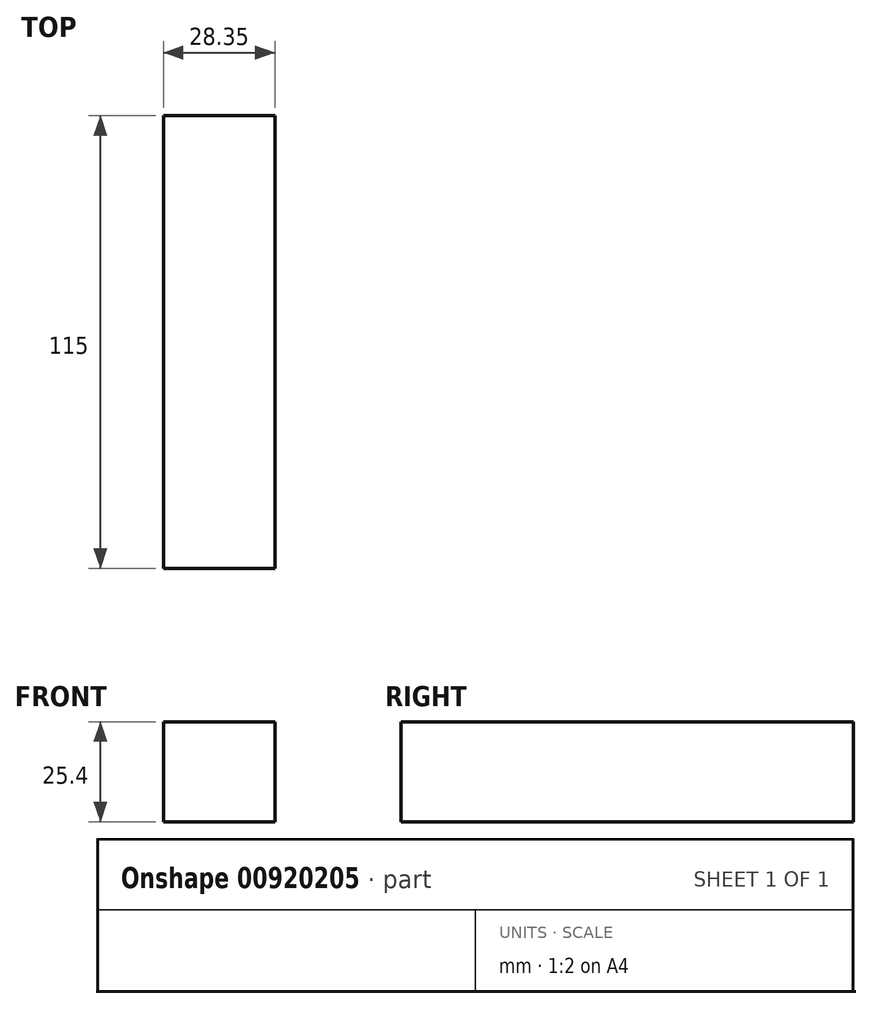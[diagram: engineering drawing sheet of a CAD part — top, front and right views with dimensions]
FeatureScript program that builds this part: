
annotation { "Feature Type Name" : "Feature", "Feature Type Description" : "" }
export const myFeature = defineFeature(function(context is Context, id is Id, definition is map)
    precondition{}
    {
        {
            var Q0;
            Q0=qCreatedBy(makeId("Top.planeOp"),FACE);
            var sketch = newSketch(context, id + "F0", { "sketchPlane" : qUnion([Q0])});
            skLineSegment(sketch, "E0.bottom", {"start": v(0, -59.79) * mm, "end": v(-28.35, -59.79) * mm});
            skLineSegment(sketch, "E0.top", {"start": v(0, 55.2) * mm, "end": v(-28.35, 55.2) * mm});
            skLineSegment(sketch, "E0.left", {"start": v(0, -59.79) * mm, "end": v(0, 55.2) * mm});
            skLineSegment(sketch, "E0.right", {"start": v(-28.35, -59.79) * mm, "end": v(-28.35, 55.2) * mm});
            skSolve(sketch);
        }
        {
            var Q0;
            Q0 = qSketchRegion(id + "F0", true);
            extrude(context, id + "F1", {"entities" : qUnion([Q0]), "depth" : 25.4 * mm, "offsetDistance" : 25.4 * mm});
        }
    });
